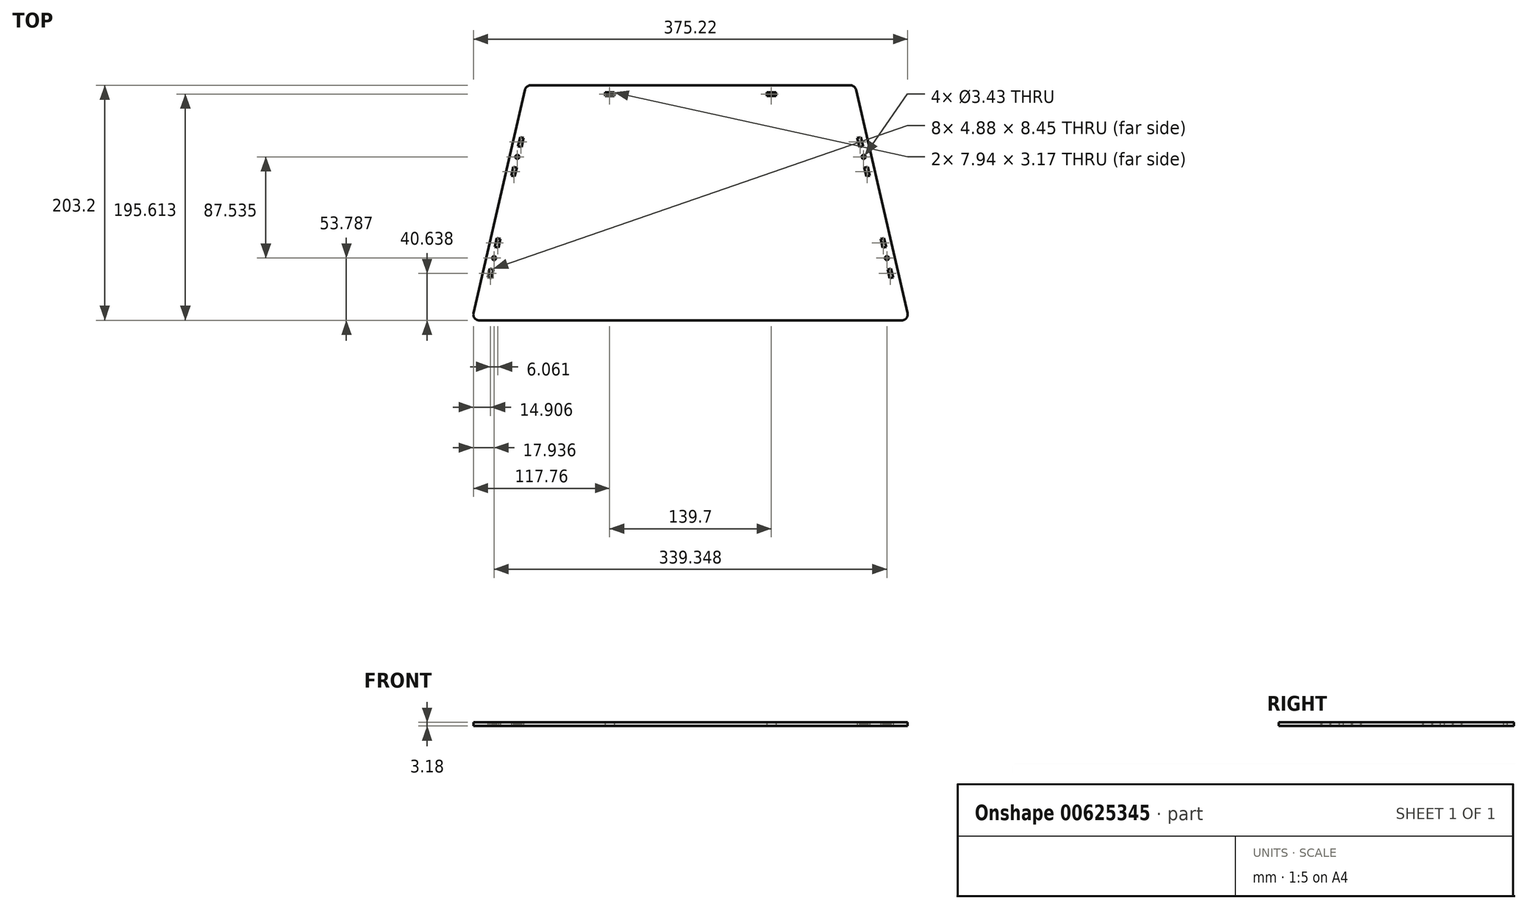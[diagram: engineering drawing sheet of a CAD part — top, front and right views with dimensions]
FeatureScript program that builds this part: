
annotation { "Feature Type Name" : "Feature", "Feature Type Description" : "" }
export const myFeature = defineFeature(function(context is Context, id is Id, definition is map)
    precondition{}
    {
        {
            var Q0;
            Q0=qCreatedBy(makeId("Top.planeOp"),FACE);
            var sketch = newSketch(context, id + "F0", { "sketchPlane" : qUnion([Q0])});
            skLineSegment(sketch, "E0", {"start": v(-188.91, -101.6) * mm, "end": v(-142.08, 101.6) * mm});
            skLineSegment(sketch, "E1", {"start": v(-142.08, 101.6) * mm, "end": v(142.08, 101.6) * mm});
            skLineSegment(sketch, "E2", {"start": v(142.08, 101.6) * mm, "end": v(188.91, -101.6) * mm});
            skLineSegment(sketch, "E3", {"start": v(188.91, -101.6) * mm, "end": v(-188.91, -101.6) * mm});
            skLineSegment(sketch, "E4", {"start": v(0, 101.6) * mm, "end": v(0, 0) * mm, "construction": true});
            skLineSegment(sketch, "E5.bottom", {"start": v(-65.88, 92.43) * mm, "end": v(-73.82, 92.43) * mm});
            skLineSegment(sketch, "E5.top", {"start": v(-65.88, 95.6) * mm, "end": v(-73.82, 95.6) * mm});
            skLineSegment(sketch, "E5.left", {"start": v(-65.88, 92.42) * mm, "end": v(-65.88, 95.6) * mm});
            skLineSegment(sketch, "E5.right", {"start": v(-73.82, 92.42) * mm, "end": v(-73.82, 95.6) * mm});
            skPoint(sketch, "E5.middle", {"position": v(-69.85, 94.01) * mm});
            skLineSegment(sketch, "E6", {"start": v(-136.87, 101.6) * mm, "end": v(-183.7, -101.6) * mm, "construction": true});
            skLineSegment(sketch, "E7", {"start": v(-148.99, 49) * mm, "end": v(-145.9, 48.3) * mm});
            skLineSegment(sketch, "E8", {"start": v(-144.11, 56.03) * mm, "end": v(-145.9, 48.3) * mm});
            skLineSegment(sketch, "E9", {"start": v(-144.11, 56.03) * mm, "end": v(-147.2, 56.74) * mm});
            skLineSegment(sketch, "E10", {"start": v(-148.99, 49) * mm, "end": v(-147.2, 56.74) * mm});
            skCircle(sketch, "E11", {"center": v(-149.58, 39.72) * mm, "radius": 1.71 * mm});
            skLineSegment(sketch, "E12", {"start": v(-147.44, 49) * mm, "end": v(-149.58, 39.72) * mm, "construction": true});
            skPoint(sketch, "E12.startSnap0", {"position": v(-147.44, 48.65) * mm});
            skLineSegment(sketch, "E13", {"start": v(-149.58, 39.72) * mm, "end": v(-156, 41.2) * mm, "construction": true});
            skLineSegment(sketch, "E14.MirrorCS", {"start": v(-151.8, 22.67) * mm, "end": v(-154.9, 23.38) * mm});
            skLineSegment(sketch, "E15.MirrorCS", {"start": v(-153.11, 31.12) * mm, "end": v(-150.02, 30.4) * mm});
            skLineSegment(sketch, "E16.MirrorCS", {"start": v(-153.11, 31.12) * mm, "end": v(-154.9, 23.38) * mm});
            skPoint(sketch, "E17.MirrorP", {"position": v(-151.57, 30.76) * mm});
            skLineSegment(sketch, "E18.MirrorCS", {"start": v(-151.8, 22.67) * mm, "end": v(-150.02, 30.4) * mm});
            skLineSegment(sketch, "E19", {"start": v(-175.14, -64.47) * mm, "end": v(-172.05, -65.19) * mm});
            skLineSegment(sketch, "E20", {"start": v(-172.05, -65.19) * mm, "end": v(-170.27, -57.45) * mm});
            skLineSegment(sketch, "E21", {"start": v(-170.27, -57.45) * mm, "end": v(-173.36, -56.74) * mm});
            skLineSegment(sketch, "E22", {"start": v(-173.36, -56.74) * mm, "end": v(-175.14, -64.47) * mm});
            skLineSegment(sketch, "E23", {"start": v(-167.3, -30.44) * mm, "end": v(-169.08, -38.18) * mm});
            skLineSegment(sketch, "E24", {"start": v(-169.08, -38.18) * mm, "end": v(-165.99, -38.89) * mm});
            skLineSegment(sketch, "E25", {"start": v(-165.99, -38.89) * mm, "end": v(-164.2, -31.15) * mm});
            skLineSegment(sketch, "E26", {"start": v(-164.2, -31.15) * mm, "end": v(-167.3, -30.44) * mm});
            skCircle(sketch, "E27", {"center": v(-169.67, -47.81) * mm, "radius": 1.71 * mm});
            skLineSegment(sketch, "E28", {"start": v(-171.81, -57.1) * mm, "end": v(-169.67, -47.81) * mm, "construction": true});
            skLineSegment(sketch, "E29", {"start": v(-169.67, -47.81) * mm, "end": v(-167.53, -38.53) * mm, "construction": true});
            skCircle(sketch, "E30.MirrorC", {"center": v(149.58, 39.72) * mm, "radius": 1.71 * mm});
            skLineSegment(sketch, "E31.MirrorCS", {"start": v(169.08, -38.18) * mm, "end": v(165.99, -38.89) * mm});
            skLineSegment(sketch, "E32.MirrorCS", {"start": v(153.11, 31.12) * mm, "end": v(150.02, 30.4) * mm});
            skCircle(sketch, "E33.MirrorC", {"center": v(169.67, -47.81) * mm, "radius": 1.71 * mm});
            skLineSegment(sketch, "E34.MirrorCS", {"start": v(169.67, -47.81) * mm, "end": v(167.53, -38.53) * mm, "construction": true});
            skLineSegment(sketch, "E35.MirrorCS", {"start": v(170.27, -57.45) * mm, "end": v(173.36, -56.74) * mm});
            skLineSegment(sketch, "E36.MirrorCS", {"start": v(165.99, -38.89) * mm, "end": v(164.2, -31.15) * mm});
            skLineSegment(sketch, "E37.MirrorCS", {"start": v(144.11, 56.03) * mm, "end": v(147.2, 56.74) * mm});
            skLineSegment(sketch, "E38.MirrorCS", {"start": v(144.11, 56.03) * mm, "end": v(145.9, 48.3) * mm});
            skLineSegment(sketch, "E39.MirrorCS", {"start": v(148.99, 49) * mm, "end": v(145.9, 48.3) * mm});
            skLineSegment(sketch, "E40.MirrorCS", {"start": v(148.99, 49) * mm, "end": v(147.2, 56.74) * mm});
            skLineSegment(sketch, "E41.MirrorCS", {"start": v(147.44, 49) * mm, "end": v(149.58, 39.72) * mm, "construction": true});
            skLineSegment(sketch, "E42.MirrorCS", {"start": v(153.11, 31.12) * mm, "end": v(154.9, 23.38) * mm});
            skLineSegment(sketch, "E43.MirrorCS", {"start": v(151.8, 22.67) * mm, "end": v(150.02, 30.4) * mm});
            skLineSegment(sketch, "E44.MirrorCS", {"start": v(164.2, -31.15) * mm, "end": v(167.3, -30.44) * mm});
            skLineSegment(sketch, "E45.MirrorCS", {"start": v(173.36, -56.74) * mm, "end": v(175.14, -64.47) * mm});
            skLineSegment(sketch, "E46.MirrorCS", {"start": v(175.14, -64.47) * mm, "end": v(172.05, -65.19) * mm});
            skLineSegment(sketch, "E47.MirrorCS", {"start": v(171.81, -57.1) * mm, "end": v(169.67, -47.81) * mm, "construction": true});
            skLineSegment(sketch, "E48.MirrorCS", {"start": v(172.05, -65.19) * mm, "end": v(170.27, -57.45) * mm});
            skLineSegment(sketch, "E49.MirrorCS", {"start": v(167.3, -30.44) * mm, "end": v(169.08, -38.18) * mm});
            skLineSegment(sketch, "E50.MirrorCS", {"start": v(151.8, 22.67) * mm, "end": v(154.9, 23.38) * mm});
            skLineSegment(sketch, "E51.MirrorCS", {"start": v(149.58, 39.72) * mm, "end": v(156, 41.2) * mm, "construction": true});
            skPoint(sketch, "E52.MirrorP", {"position": v(147.44, 48.65) * mm});
            skPoint(sketch, "E53.MirrorP", {"position": v(151.57, 30.76) * mm});
            skPoint(sketch, "E54.MirrorP", {"position": v(69.85, 94.01) * mm});
            skLineSegment(sketch, "E55.MirrorCS", {"start": v(65.88, 92.43) * mm, "end": v(73.82, 92.43) * mm});
            skLineSegment(sketch, "E56.MirrorCS", {"start": v(65.88, 95.6) * mm, "end": v(73.82, 95.6) * mm});
            skLineSegment(sketch, "E57.MirrorCS", {"start": v(65.88, 92.42) * mm, "end": v(65.88, 95.6) * mm});
            skLineSegment(sketch, "E58.MirrorCS", {"start": v(73.82, 92.42) * mm, "end": v(73.82, 95.6) * mm});
            skSolve(sketch);
        }
        {
            var Q0;
            Q0 = qSketchRegion(id + "F0", true);
            extrude(context, id + "F1", {"entities" : qUnion([Q0]), "depth" : 3.17 * mm, "offsetDistance" : 25.4 * mm});
        }
        {
            var Q0;
            Q0=makeQuery(id+"F1.opExtrude","SWEPT_EDGE",EDGE,{"disambiguationData":[OSD([sQuery(id+"F0.wireOp",EDGE,"E0"),sQuery(id+"F0.wireOp",EDGE,"E1")])]});
            var Q1;
            Q1=makeQuery(id+"F1.opExtrude","SWEPT_EDGE",EDGE,{"disambiguationData":[OSD([sQuery(id+"F0.wireOp",EDGE,"E0"),sQuery(id+"F0.wireOp",EDGE,"E3")])]});
            var Q2;
            Q2=makeQuery(id+"F1.opExtrude","SWEPT_EDGE",EDGE,{"disambiguationData":[OSD([sQuery(id+"F0.wireOp",EDGE,"E1"),sQuery(id+"F0.wireOp",EDGE,"E2")])]});
            var Q3;
            Q3=makeQuery(id+"F1.opExtrude","SWEPT_EDGE",EDGE,{"disambiguationData":[OSD([sQuery(id+"F0.wireOp",EDGE,"E2"),sQuery(id+"F0.wireOp",EDGE,"E3")])]});
            fillet(context, id + "F2", {"entities" : qUnion([Q0, Q1, Q2, Q3]), "radius" : 5.08 * mm, "tangentPropagation" : true, "allowEdgeOverflow" : false});
        }
    });
